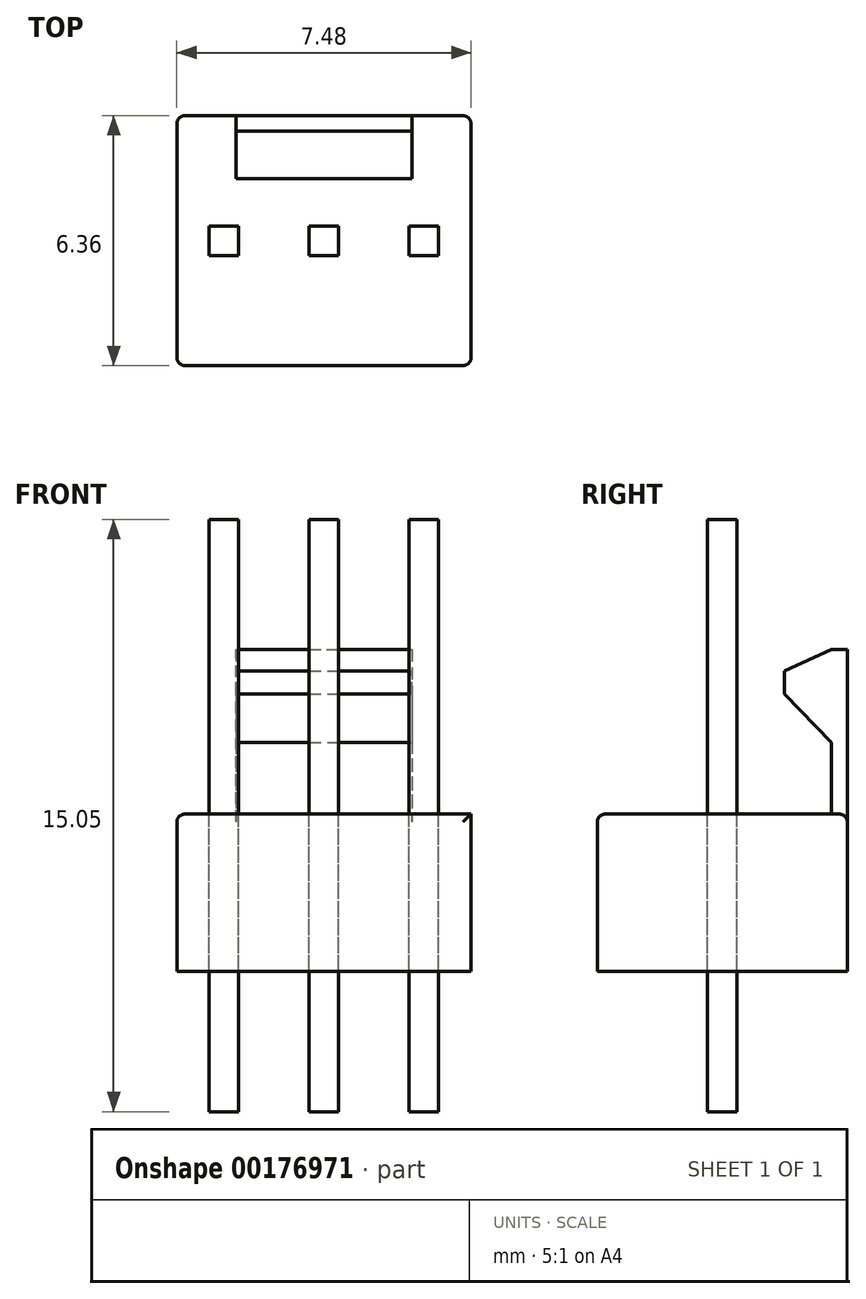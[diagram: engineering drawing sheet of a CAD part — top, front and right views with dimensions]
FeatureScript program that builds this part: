
annotation { "Feature Type Name" : "Feature", "Feature Type Description" : "" }
export const myFeature = defineFeature(function(context is Context, id is Id, definition is map)
    precondition{}
    {
        {
            var Q0;
            Q0=qCreatedBy(makeId("Top.planeOp"),FACE);
            var sketch = newSketch(context, id + "F0", { "sketchPlane" : qUnion([Q0])});
            skLineSegment(sketch, "E0.bottom", {"start": v(-3.74, 3.17) * mm, "end": v(3.73, 3.17) * mm});
            skLineSegment(sketch, "E0.top", {"start": v(-3.74, -3.18) * mm, "end": v(3.73, -3.17) * mm});
            skLineSegment(sketch, "E0.left", {"start": v(-3.74, 3.17) * mm, "end": v(-3.74, -3.18) * mm});
            skLineSegment(sketch, "E0.right", {"start": v(3.73, 3.18) * mm, "end": v(3.73, -3.17) * mm});
            skSolve(sketch);
        }
        {
            var Q0;
            Q0=makeQuery(id+"F0.imprint","IMPRINT",FACE,{"disambiguationData":[TD([[makeQuery(id+"F0.imprint","IMPRINT",EDGE,{"derivedFrom":sQuery(id+"F0.wireOp",EDGE,"E0.bottom")}),-1.0]])]});
            extrude(context, id + "F1", {"entities" : qUnion([Q0]), "depth" : 4 * mm});
        }
        {
            var Q0;
            Q0=makeQuery(id+"F1.opExtrude","SWEPT_FACE",FACE,{"disambiguationData":[OSD([sQuery(id+"F0.wireOp",EDGE,"E0.right")])]});
            var sketch = newSketch(context, id + "F2", { "sketchPlane" : qUnion([Q0])});
            skLineSegment(sketch, "E1.bottom", {"start": v(3.18, 4) * mm, "end": v(1.57, 4) * mm});
            skLineSegment(sketch, "E1.top", {"start": v(3.18, 8.18) * mm, "end": v(1.57, 8.18) * mm});
            skLineSegment(sketch, "E1.left", {"start": v(3.18, 4) * mm, "end": v(3.18, 8.18) * mm});
            skLineSegment(sketch, "E1.right", {"start": v(1.57, 4) * mm, "end": v(1.57, 8.18) * mm});
            skSolve(sketch);
        }
        {
            var Q0;
            Q0=makeQuery(id+"F2.imprint","IMPRINT",FACE,{"disambiguationData":[TD([[makeQuery(id+"F2.imprint","IMPRINT",EDGE,{"derivedFrom":sQuery(id+"F2.wireOp",EDGE,"E1.bottom")}),-1.0]])]});
            extrude(context, id + "F3", {"entities" : qUnion([Q0]), "operationType" : NewBodyOperationType.ADD, "oppositeDirection" : true, "depth" : 1.5 * mm});
        }
        {
            var Q0;
            Q0=makeQuery(id+"F3.opExtrude","CAP_FACE",FACE,{"disambiguationData":[OSD([sQuery(id+"F2.wireOp",EDGE,"E1.bottom"),sQuery(id+"F2.wireOp",EDGE,"E1.top"),sQuery(id+"F2.wireOp",EDGE,"E1.left"),sQuery(id+"F2.wireOp",EDGE,"E1.right")])],"isStart":false});
            var sketch = newSketch(context, id + "F4", { "sketchPlane" : qUnion([Q0])});
            skLineSegment(sketch, "E2", {"start": v(-3.17, 4) * mm, "end": v(-3.18, 8.18) * mm});
            skLineSegment(sketch, "E3", {"start": v(-3.18, 8.18) * mm, "end": v(-2.78, 8.18) * mm});
            skLineSegment(sketch, "E4", {"start": v(-2.78, 8.18) * mm, "end": v(-1.57, 7.63) * mm});
            skLineSegment(sketch, "E5", {"start": v(-1.57, 7.63) * mm, "end": v(-1.57, 7.05) * mm});
            skLineSegment(sketch, "E6", {"start": v(-1.57, 7.05) * mm, "end": v(-2.78, 5.83) * mm});
            skLineSegment(sketch, "E7", {"start": v(-2.78, 5.83) * mm, "end": v(-2.78, 4) * mm});
            skLineSegment(sketch, "E8", {"start": v(-2.78, 4) * mm, "end": v(-3.17, 4) * mm});
            skSolve(sketch);
        }
        {
            var Q0;
            Q0 = qSketchRegion(id + "F4", true);
            extrude(context, id + "F5", {"entities" : qUnion([Q0]), "operationType" : NewBodyOperationType.ADD, "depth" : 4.47 * mm});
        }
        {
            var Q0;
            Q0=makeQuery(id+"F5.boolean.opBoolean","MERGE",FACE,{"derivedFrom":[makeQuery(id+"F3.opExtrude","SWEPT_FACE",FACE,{"disambiguationData":[OSD([sQuery(id+"F2.wireOp",EDGE,"E1.right")])]}),makeQuery(id+"F5.opExtrude","SWEPT_FACE",FACE,{"disambiguationData":[OSD([sQuery(id+"F4.wireOp",EDGE,"E5")])]})]});
            var sketch = newSketch(context, id + "F6", { "sketchPlane" : qUnion([Q0])});
            skLineSegment(sketch, "E9.bottom", {"start": v(3.73, 8.18) * mm, "end": v(2.23, 8.18) * mm});
            skLineSegment(sketch, "E9.top", {"start": v(3.73, 4) * mm, "end": v(2.23, 4) * mm});
            skLineSegment(sketch, "E9.left", {"start": v(3.73, 8.18) * mm, "end": v(3.73, 4) * mm});
            skLineSegment(sketch, "E9.right", {"start": v(2.23, 8.18) * mm, "end": v(2.23, 4) * mm});
            skSolve(sketch);
        }
        {
            var Q0;
            Q0 = qSketchRegion(id + "F6", true);
            extrude(context, id + "F7", {"entities" : qUnion([Q0]), "operationType" : NewBodyOperationType.REMOVE, "oppositeDirection" : true, "depth" : 25 * mm});
        }
        {
            var Q0;
            Q0=makeQuery(id+"F1.opExtrude","CAP_EDGE",EDGE,{"disambiguationData":[OSD([sQuery(id+"F0.wireOp",EDGE,"E0.left")])],"isStart":false});
            var Q1;
            Q1=makeQuery(id+"F1.opExtrude","CAP_EDGE",EDGE,{"disambiguationData":[OSD([sQuery(id+"F0.wireOp",EDGE,"E0.bottom")])],"isStart":false});
            var Q2;
            Q2=makeQuery(id+"F7.boolean.opBoolean","INTERSECT",EDGE,{"derivedFrom":[makeQuery(id+"F5.boolean.opBoolean","MERGE",FACE,{"derivedFrom":[makeQuery(id+"F3.boolean.opBoolean","MERGE",FACE,{"derivedFrom":[makeQuery(id+"F1.opExtrude","SWEPT_FACE",FACE,{"disambiguationData":[OSD([sQuery(id+"F0.wireOp",EDGE,"E0.bottom")])]}),makeQuery(id+"F3.opExtrude","SWEPT_FACE",FACE,{"disambiguationData":[OSD([sQuery(id+"F2.wireOp",EDGE,"E1.left")])]})]}),makeQuery(id+"F5.opExtrude","SWEPT_FACE",FACE,{"disambiguationData":[OSD([sQuery(id+"F4.wireOp",EDGE,"E2")])]})]}),makeQuery(id+"F7.opExtrude","SWEPT_FACE",FACE,{"disambiguationData":[OSD([sQuery(id+"F6.wireOp",EDGE,"E9.top")])]})]});
            var Q3;
            Q3=makeQuery(id+"F7.boolean.opBoolean","MERGE",EDGE,{"derivedFrom":[makeQuery(id+"F1.opExtrude","CAP_EDGE",EDGE,{"disambiguationData":[OSD([sQuery(id+"F0.wireOp",EDGE,"E0.right")])],"isStart":false}),makeQuery(id+"F7.opExtrude","SWEPT_EDGE",EDGE,{"disambiguationData":[OSD([sQuery(id+"F6.wireOp",EDGE,"E9.top"),sQuery(id+"F6.wireOp",EDGE,"E9.left")])]})]});
            var Q4;
            Q4=makeQuery(id+"F1.opExtrude","CAP_EDGE",EDGE,{"disambiguationData":[OSD([sQuery(id+"F0.wireOp",EDGE,"E0.top")])],"isStart":false});
            var Q5;
            Q5=makeQuery(id+"F1.opExtrude","SWEPT_EDGE",EDGE,{"disambiguationData":[OSD([sQuery(id+"F0.wireOp",EDGE,"E0.top"),sQuery(id+"F0.wireOp",EDGE,"E0.left")])]});
            var Q6;
            Q6=makeQuery(id+"F1.opExtrude","SWEPT_EDGE",EDGE,{"disambiguationData":[OSD([sQuery(id+"F0.wireOp",EDGE,"E0.top"),sQuery(id+"F0.wireOp",EDGE,"E0.right")])]});
            var Q7;
            Q7=makeQuery(id+"F1.opExtrude","SWEPT_EDGE",EDGE,{"disambiguationData":[OSD([sQuery(id+"F0.wireOp",EDGE,"E0.bottom"),sQuery(id+"F0.wireOp",EDGE,"E0.left")])]});
            var Q8;
            Q8=makeQuery(id+"F3.boolean.opBoolean","MERGE",EDGE,{"derivedFrom":[makeQuery(id+"F1.opExtrude","SWEPT_EDGE",EDGE,{"disambiguationData":[OSD([sQuery(id+"F0.wireOp",EDGE,"E0.bottom"),sQuery(id+"F0.wireOp",EDGE,"E0.right")])]}),makeQuery(id+"F3.opExtrude","CAP_EDGE",EDGE,{"disambiguationData":[OSD([sQuery(id+"F2.wireOp",EDGE,"E1.left")])],"isStart":true})]});
            fillet(context, id + "F8", {"entities" : qUnion([Q0, Q1, Q2, Q3, Q4, Q5, Q6, Q7, Q8]), "radius" : .2 * mm, "tangentPropagation" : true, "allowEdgeOverflow" : false});
        }
        {
            var Q0;
            Q0=makeQuery(id+"F7.boolean.opBoolean","MERGE",FACE,{"derivedFrom":[makeQuery(id+"F1.opExtrude","CAP_FACE",FACE,{"disambiguationData":[OSD([sQuery(id+"F0.wireOp",EDGE,"E0.bottom"),sQuery(id+"F0.wireOp",EDGE,"E0.top"),sQuery(id+"F0.wireOp",EDGE,"E0.left"),sQuery(id+"F0.wireOp",EDGE,"E0.right")])],"isStart":false}),makeQuery(id+"F7.opExtrude","SWEPT_FACE",FACE,{"disambiguationData":[OSD([sQuery(id+"F6.wireOp",EDGE,"E9.top")])]})]});
            var sketch = newSketch(context, id + "F9", { "sketchPlane" : qUnion([Q0])});
            skLineSegment(sketch, "E10.bottom", {"start": v(-0.37, 0.37) * mm, "end": v(0.38, 0.38) * mm});
            skLineSegment(sketch, "E10.top", {"start": v(-0.37, -0.38) * mm, "end": v(0.38, -0.37) * mm});
            skLineSegment(sketch, "E10.left", {"start": v(-0.37, 0.37) * mm, "end": v(-0.37, -0.38) * mm});
            skLineSegment(sketch, "E10.right", {"start": v(0.38, 0.38) * mm, "end": v(0.38, -0.37) * mm});
            skLineSegment(sketch, "E11.bottom", {"start": v(2.17, 0.38) * mm, "end": v(2.92, 0.38) * mm});
            skLineSegment(sketch, "E11.top", {"start": v(2.17, -0.37) * mm, "end": v(2.92, -0.37) * mm});
            skLineSegment(sketch, "E11.left", {"start": v(2.17, 0.37) * mm, "end": v(2.17, -0.37) * mm});
            skLineSegment(sketch, "E11.right", {"start": v(2.92, 0.38) * mm, "end": v(2.92, -0.37) * mm});
            skLineSegment(sketch, "E12.MirrorCS", {"start": v(-2.17, 0.38) * mm, "end": v(-2.92, 0.38) * mm});
            skLineSegment(sketch, "E13.MirrorCS", {"start": v(-2.17, -0.37) * mm, "end": v(-2.92, -0.37) * mm});
            skLineSegment(sketch, "E14.MirrorCS", {"start": v(-2.92, 0.38) * mm, "end": v(-2.92, -0.37) * mm});
            skLineSegment(sketch, "E15.MirrorCS", {"start": v(-2.17, 0.37) * mm, "end": v(-2.17, -0.37) * mm});
            skSolve(sketch);
        }
        {
            var Q0;
            Q0 = qSketchRegion(id + "F9", true);
            extrude(context, id + "F10", {"entities" : qUnion([Q0]), "depth" : 7.5 * mm});
        }
        {
            var Q0;
            Q0 = qSketchRegion(id + "F9", true);
            extrude(context, id + "F11", {"entities" : qUnion([Q0]), "oppositeDirection" : true, "depth" : 7.56 * mm});
        }
    });
